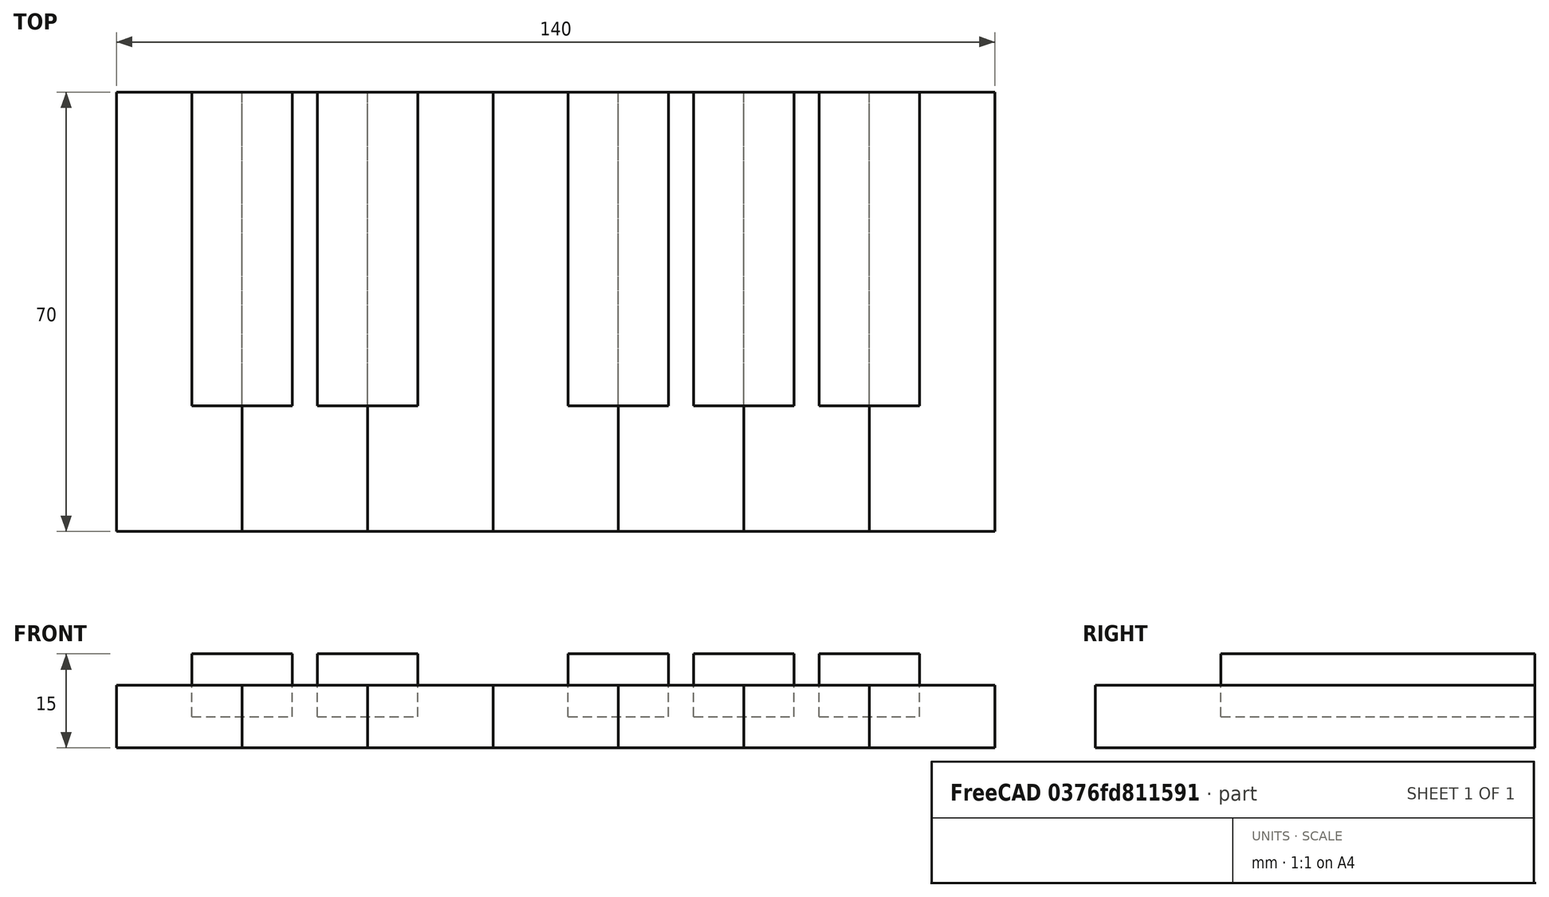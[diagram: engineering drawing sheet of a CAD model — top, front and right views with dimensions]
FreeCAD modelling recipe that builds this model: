
FCSTD DOCUMENT  (FreeCAD 0.19R)
Label: piano-board
License: All rights reserved
LicenseURL: http://en.wikipedia.org/wiki/All_rights_reserved
objects: Part::Box×12, App::FeaturePython×1
note: 12 computed .brp shape members not serialized (recipe doc carries the construction recipe); baked Part::Feature solids carry a one-line shape summary decoded from their .brp

FEATURE [Part::Box] Box  label="C"
  AttacherType = Attacher::AttachEngine3D
  Height = 10
  Length = 20
  Width = 70
FEATURE [Part::Box] Box001  label="D"
  AttacherType = Attacher::AttachEngine3D
  Height = 10
  Length = 20
  Placement = pos=(20,0,0) rot=(0,0,1;0rad)
  Width = 70
FEATURE [Part::Box] Box002  label="E"
  AttacherType = Attacher::AttachEngine3D
  Height = 10
  Length = 20
  Placement = pos=(40,0,0) rot=(0,0,1;0rad)
  Width = 70
FEATURE [Part::Box] Box003  label="F"
  AttacherType = Attacher::AttachEngine3D
  Height = 10
  Length = 20
  Placement = pos=(60,0,0) rot=(0,0,1;0rad)
  Width = 70
FEATURE [Part::Box] Box004  label="G"
  AttacherType = Attacher::AttachEngine3D
  Height = 10
  Length = 20
  Placement = pos=(80,0,0) rot=(0,0,1;0rad)
  Width = 70
FEATURE [Part::Box] Box005  label="A"
  AttacherType = Attacher::AttachEngine3D
  Height = 10
  Length = 20
  Placement = pos=(100,0,0) rot=(0,0,1;0rad)
  Width = 70
FEATURE [Part::Box] Box006  label="B"
  AttacherType = Attacher::AttachEngine3D
  Height = 10
  Length = 20
  Placement = pos=(120,0,0) rot=(0,0,1;0rad)
  Width = 70
FEATURE [Part::Box] Box007  label="C#"
  AttacherType = Attacher::AttachEngine3D
  Height = 10
  Length = 16
  Placement = pos=(12,20,5) rot=(0,0,1;0rad)
  Width = 50
FEATURE [Part::Box] Box008  label="D#"
  AttacherType = Attacher::AttachEngine3D
  Height = 10
  Length = 16
  Placement = pos=(32,20,5) rot=(0,0,1;0rad)
  Width = 50
FEATURE [Part::Box] Box009  label="F#"
  AttacherType = Attacher::AttachEngine3D
  Height = 10
  Length = 16
  Placement = pos=(72,20,5) rot=(0,0,1;0rad)
  Width = 50
FEATURE [Part::Box] Box010  label="G#"
  AttacherType = Attacher::AttachEngine3D
  Height = 10
  Length = 16
  Placement = pos=(92,20,5) rot=(0,0,1;0rad)
  Width = 50
FEATURE [Part::Box] Box011  label="A#"
  AttacherType = Attacher::AttachEngine3D
  Height = 10
  Length = 16
  Placement = pos=(112,20,5) rot=(0,0,1;0rad)
  Width = 50
FEATURE [App::FeaturePython] PDInclude  # WARN: FeaturePython — macro-defined, semantics opaque (R4)
